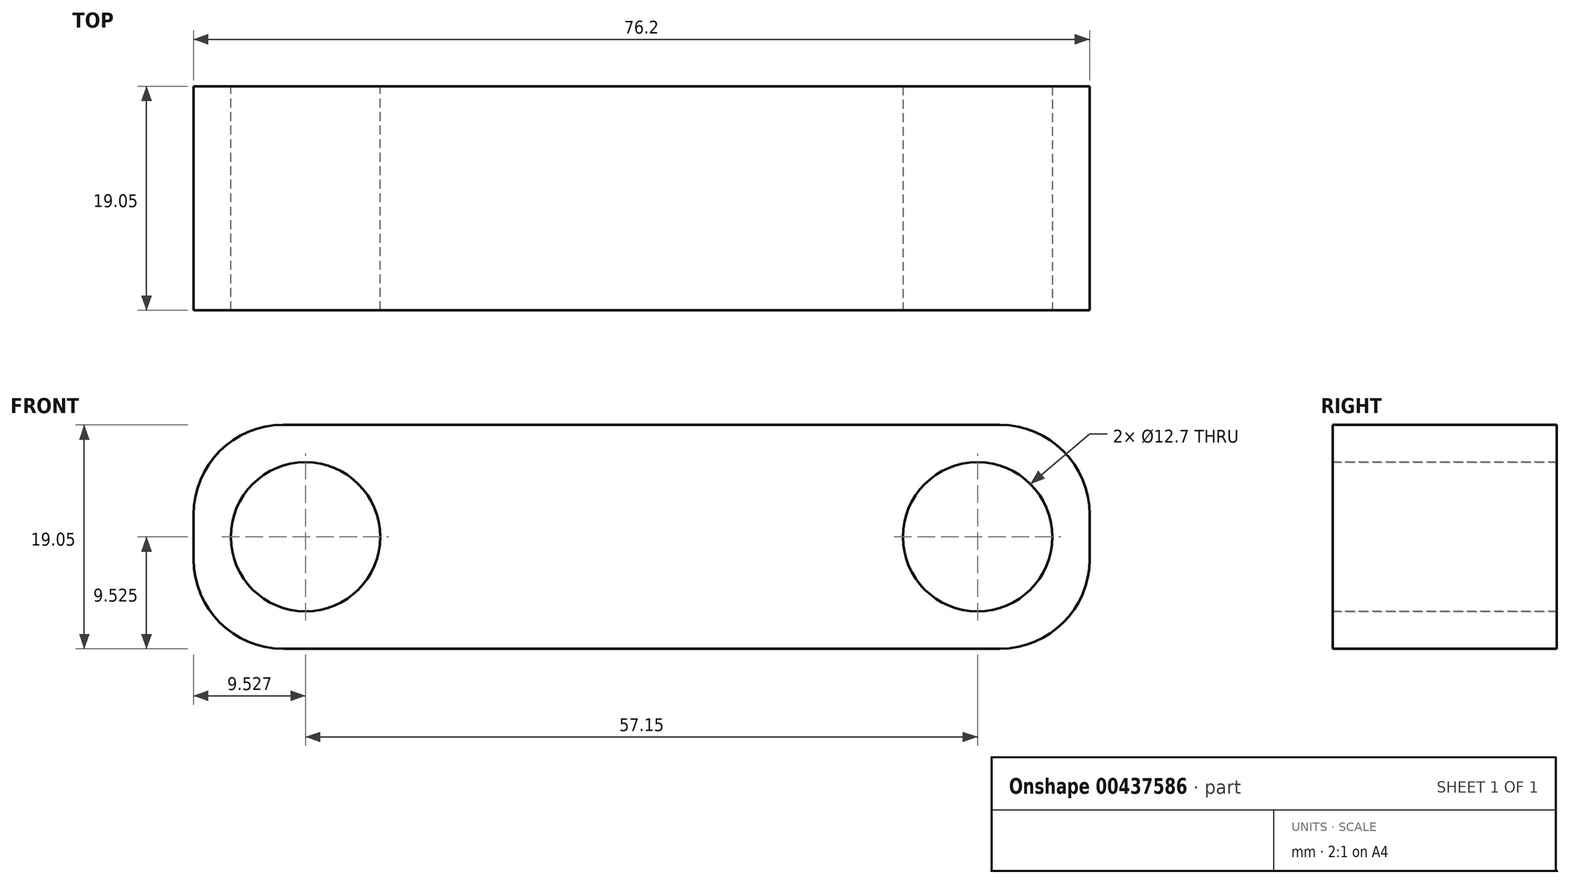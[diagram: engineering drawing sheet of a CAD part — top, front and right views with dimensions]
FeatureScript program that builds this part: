
annotation { "Feature Type Name" : "Feature", "Feature Type Description" : "" }
export const myFeature = defineFeature(function(context is Context, id is Id, definition is map)
    precondition{}
    {
        {
            var Q0;
            Q0=qCreatedBy(makeId("Top.planeOp"),FACE);
            var sketch = newSketch(context, id + "F0", { "sketchPlane" : qUnion([Q0])});
            skLineSegment(sketch, "E0.bottom", {"start": v(-28.48, 5.03) * mm, "end": v(47.72, 5.03) * mm});
            skLineSegment(sketch, "E0.top", {"start": v(-28.48, -14.02) * mm, "end": v(47.72, -14.02) * mm});
            skLineSegment(sketch, "E0.left", {"start": v(-28.48, 5.03) * mm, "end": v(-28.48, -14.02) * mm});
            skLineSegment(sketch, "E0.right", {"start": v(47.72, 5.03) * mm, "end": v(47.72, -14.02) * mm});
            skSolve(sketch);
        }
        {
            var Q0;
            Q0=makeQuery(id+"F0.imprint","IMPRINT",FACE,{"disambiguationData":[TD([[makeQuery(id+"F0.imprint","IMPRINT",EDGE,{"derivedFrom":sQuery(id+"F0.wireOp",EDGE,"E0.bottom")}),-1.0]])]});
            extrude(context, id + "F1", {"entities" : qUnion([Q0]), "depth" : 19.05 * mm});
        }
        {
            var Q0;
            Q0=makeQuery(id+"F1.opExtrude","SWEPT_FACE",FACE,{"disambiguationData":[OSD([sQuery(id+"F0.wireOp",EDGE,"E0.bottom")])]});
            var sketch = newSketch(context, id + "F2", { "sketchPlane" : qUnion([Q0])});
            skPoint(sketch, "E1", {"position": v(18.95, 9.53) * mm});
            skSolve(sketch);
        }
        {
            var Q0;
            Q0=sQuery(id+"F2.wireOp",VERTEX,"E1");
            var Q1;
            Q1=makeQuery(id+"F1.opExtrude","SWEPT_BODY",BODY,{"disambiguationData":[OSD([sQuery(id+"F0.wireOp",EDGE,"E0.bottom"),sQuery(id+"F0.wireOp",EDGE,"E0.top"),sQuery(id+"F0.wireOp",EDGE,"E0.left"),sQuery(id+"F0.wireOp",EDGE,"E0.right")])]});
            hole(context, id + "F3", {"style" : HoleStyle.SIMPLE, "endStyle" : HoleEndStyle.THROUGH, "holeDiameter" : 12.7 * mm, "isTappedThrough" : true, "tappedDepth" : 12.7 * mm, "tapClearance" : 3, "locations" : qUnion([Q0]), "scope" : qUnion([Q1])});
        }
        {
            var Q0;
            Q0=makeQuery(id+"F1.opExtrude","SWEPT_FACE",FACE,{"disambiguationData":[OSD([sQuery(id+"F0.wireOp",EDGE,"E0.top")])]});
            var sketch = newSketch(context, id + "F4", { "sketchPlane" : qUnion([Q0])});
            skPoint(sketch, "E2", {"position": v(38.2, 9.53) * mm});
            skSolve(sketch);
        }
        {
            var Q0;
            Q0=sQuery(id+"F4.wireOp",VERTEX,"E2");
            var Q1;
            Q1=makeQuery(id+"F1.opExtrude","SWEPT_BODY",BODY,{"disambiguationData":[OSD([sQuery(id+"F0.wireOp",EDGE,"E0.bottom"),sQuery(id+"F0.wireOp",EDGE,"E0.top"),sQuery(id+"F0.wireOp",EDGE,"E0.left"),sQuery(id+"F0.wireOp",EDGE,"E0.right")])]});
            hole(context, id + "F5", {"style" : HoleStyle.SIMPLE, "endStyle" : HoleEndStyle.THROUGH, "holeDiameter" : 12.7 * mm, "isTappedThrough" : true, "tappedDepth" : 12.7 * mm, "tapClearance" : 3, "startFromSketch" : true, "locations" : qUnion([Q0]), "scope" : qUnion([Q1])});
        }
        {
            var Q0;
            Q0=makeQuery(id+"F1.opExtrude","CAP_EDGE",EDGE,{"disambiguationData":[OSD([sQuery(id+"F0.wireOp",EDGE,"E0.right")])],"isStart":false});
            var Q1;
            Q1=makeQuery(id+"F1.opExtrude","CAP_EDGE",EDGE,{"disambiguationData":[OSD([sQuery(id+"F0.wireOp",EDGE,"E0.right")])],"isStart":true});
            var Q2;
            Q2=makeQuery(id+"F1.opExtrude","CAP_EDGE",EDGE,{"disambiguationData":[OSD([sQuery(id+"F0.wireOp",EDGE,"E0.left")])],"isStart":false});
            var Q3;
            Q3=makeQuery(id+"F1.opExtrude","CAP_EDGE",EDGE,{"disambiguationData":[OSD([sQuery(id+"F0.wireOp",EDGE,"E0.left")])],"isStart":true});
            fillet(context, id + "F6", {"entities" : qUnion([Q0, Q1, Q2, Q3]), "radius" : 7.62 * mm, "tangentPropagation" : true, "allowEdgeOverflow" : false});
        }
    });
